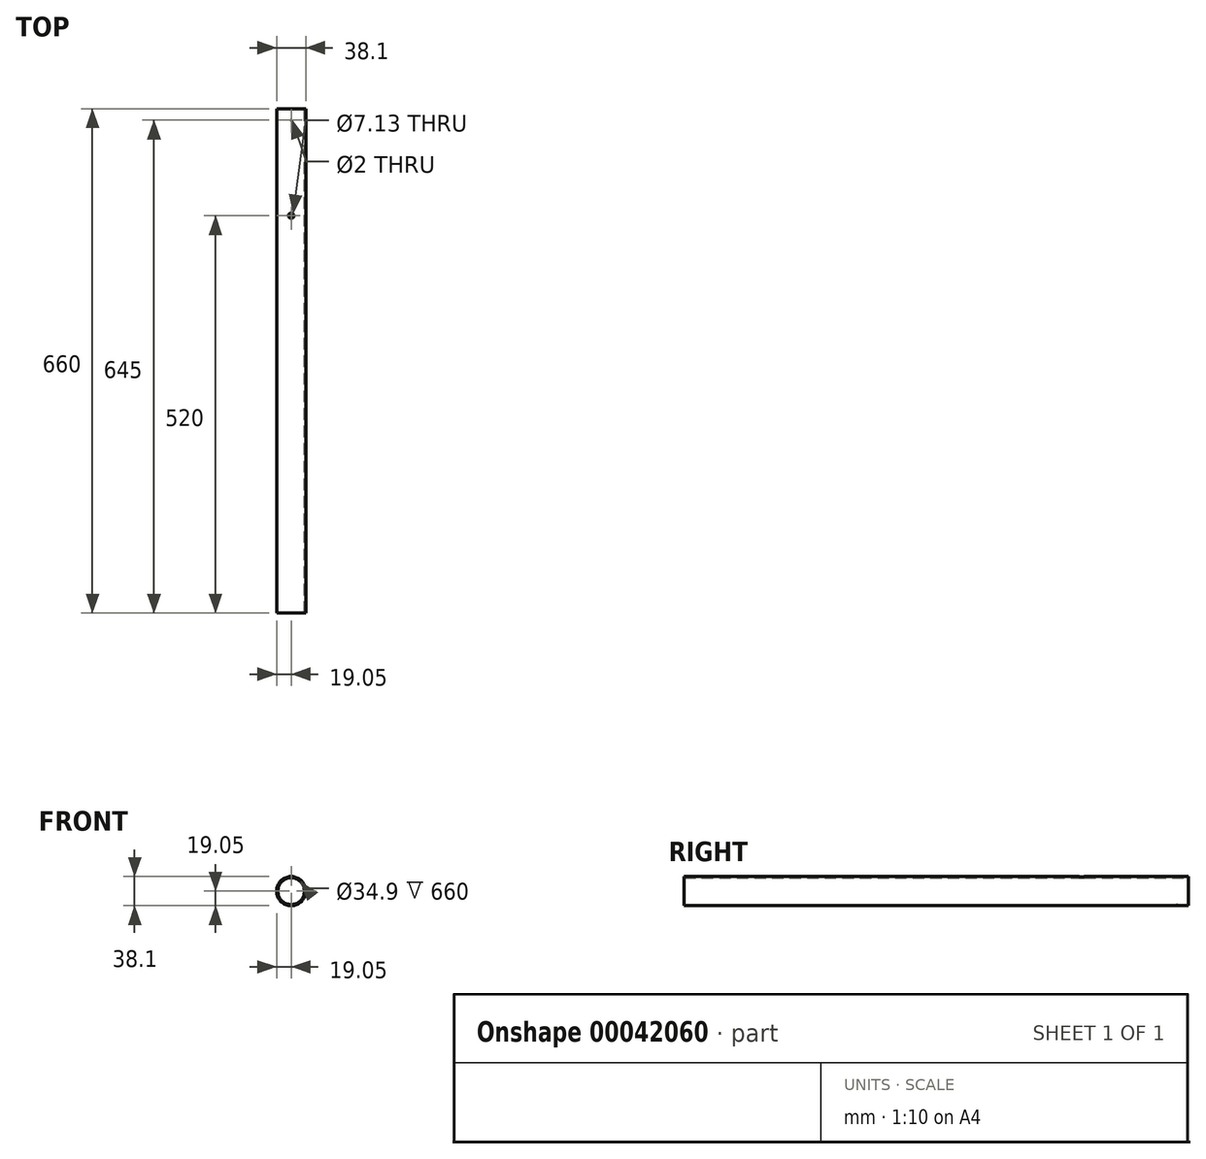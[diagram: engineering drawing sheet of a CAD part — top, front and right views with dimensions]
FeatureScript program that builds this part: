
annotation { "Feature Type Name" : "Feature", "Feature Type Description" : "" }
export const myFeature = defineFeature(function(context is Context, id is Id, definition is map)
    precondition{}
    {
        {
            var Q0;
            Q0=qCreatedBy(makeId("Front.planeOp"),FACE);
            var sketch = newSketch(context, id + "F0", { "sketchPlane" : qUnion([Q0])});
            skCircle(sketch, "E0", {"center": v(0, 0) * mm, "radius": 19.05 * mm});
            skCircle(sketch, "E1.0", {"center": v(0, 0) * mm, "radius": 17.45 * mm});
            skSolve(sketch);
        }
        {
            var Q0;
            Q0=makeQuery(id+"F0.imprint","IMPRINT",FACE,{"disambiguationData":[TD([[makeQuery(id+"F0.imprint","IMPRINT",EDGE,{"derivedFrom":sQuery(id+"F0.wireOp",EDGE,"E0")}),1.0]])]});
            extrude(context, id + "F1", {"entities" : qUnion([Q0]), "depth" : 660 * mm});
        }
        {
            var Q0;
            Q0=qCreatedBy(makeId("Top.planeOp"),FACE);
            var sketch = newSketch(context, id + "F2", { "sketchPlane" : qUnion([Q0])});
            skCircle(sketch, "E2", {"center": v(0, -140) * mm, "radius": 3.56 * mm});
            skSolve(sketch);
        }
        {
            var Q0;
            Q0=qSketchRegion(id+"F2",true);
            var Q1;
            Q1=makeQuery(id+"F1.opExtrude","SWEPT_FACE",FACE,{"disambiguationData":[OSD([sQuery(id+"F0.wireOp",EDGE,"E0")])]});
            extrude(context, id + "F3", {"entities" : qUnion([Q0]), "operationType" : NewBodyOperationType.REMOVE, "endBound" : BoundingType.UP_TO_SURFACE, "endBoundEntityFace" : qUnion([Q1]), "depth" : 25 * mm});
        }
        {
            var Q0;
            Q0=qCreatedBy(makeId("Top.planeOp"),FACE);
            var sketch = newSketch(context, id + "F4", { "sketchPlane" : qUnion([Q0])});
            skCircle(sketch, "E3", {"center": v(0, -15) * mm, "radius": 1 * mm});
            skSolve(sketch);
        }
        {
            var Q0;
            Q0=qSketchRegion(id+"F4",true);
            var Q1;
            Q1=makeQuery(id+"F1.opExtrude","SWEPT_FACE",FACE,{"disambiguationData":[OSD([sQuery(id+"F0.wireOp",EDGE,"E0")])]});
            extrude(context, id + "F5", {"entities" : qUnion([Q0]), "operationType" : NewBodyOperationType.REMOVE, "endBound" : BoundingType.UP_TO_SURFACE, "oppositeDirection" : true, "endBoundEntityFace" : qUnion([Q1]), "depth" : 25 * mm});
        }
    });
